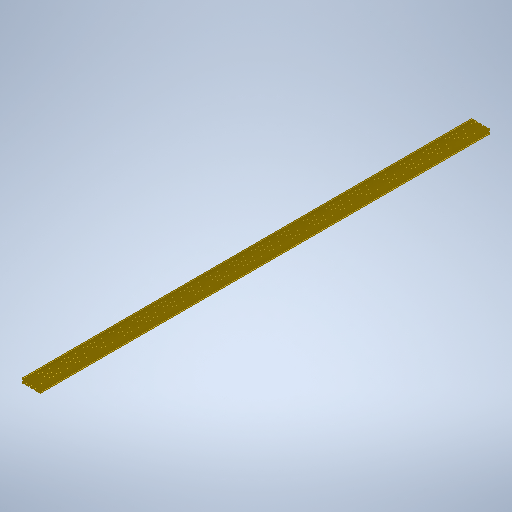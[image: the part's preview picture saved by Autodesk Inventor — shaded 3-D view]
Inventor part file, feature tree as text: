
AUTODESK INVENTOR PART (.ipt)
format: ipt  version: 2025.2 (Build 292293000, 293)  size: 578,560 bytes
history: native  units: mm
features: mirror x2, extrude x1, fillet x1, sketch x1
ambient origin geometry x8: Origin, YZ Plane, XZ Plane, XY Plane, X Axis, Y Axis, Z Axis, Center Point
bodies: Body1 (feature_tree)
feature tree (5):
  extrude  "Extrusão3"  Depth=10.0mm
  mirror  "Espelhar7"
  mirror  "Espelhar8"
  fillet  "Arredondamento5"  Radius=20.0mm
  sketch  "Esboço3"  dims[d45=80.0mm d46=10.0mm d47=20.0mm d48=6.2mm d49=5.0mm d51=6.0mm d54=0.5mm d56=2.0mm d57=0.5mm d59=4.0mm d67=1.5mm d68=2000.0mm d69=0.0mm d70=1.0mm]
